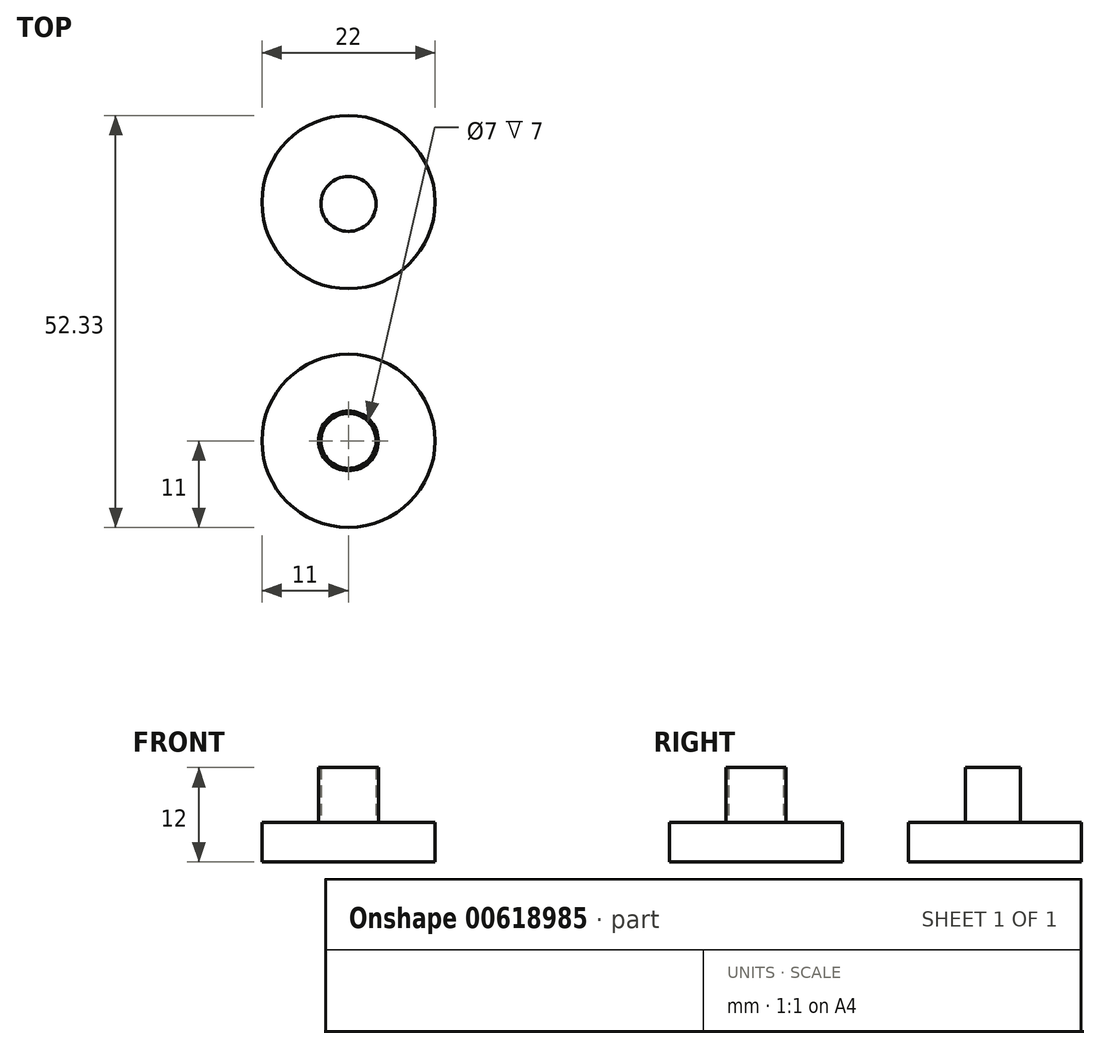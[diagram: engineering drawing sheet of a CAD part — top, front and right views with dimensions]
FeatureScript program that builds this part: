
annotation { "Feature Type Name" : "Feature", "Feature Type Description" : "" }
export const myFeature = defineFeature(function(context is Context, id is Id, definition is map)
    precondition{}
    {
        {
            var Q0;
            Q0=qCreatedBy(makeId("Top.planeOp"),FACE);
            var sketch = newSketch(context, id + "F0", { "sketchPlane" : qUnion([Q0])});
            skCircle(sketch, "E0", {"center": v(0, 0) * mm, "radius": 11 * mm});
            skCircle(sketch, "E1", {"center": v(0, 30.33) * mm, "radius": 11 * mm});
            skSolve(sketch);
        }
        {
            var Q0;
            Q0 = qSketchRegion(id + "F0", true);
            extrude(context, id + "F1", {"entities" : qUnion([Q0]), "depth" : 5 * mm, "offsetDistance" : 25 * mm});
        }
        {
            var Q0;
            Q0=qCreatedBy(makeId("Top.planeOp"),FACE);
            var sketch = newSketch(context, id + "F2", { "sketchPlane" : qUnion([Q0])});
            skCircle(sketch, "E2", {"center": v(0, 0) * mm, "radius": 3.8 * mm});
            skCircle(sketch, "E3", {"center": v(0, 0) * mm, "radius": 3.5 * mm});
            skSolve(sketch);
        }
        {
            var Q0;
            Q0 = qSketchRegion(id + "F2", true);
            extrude(context, id + "F3", {"entities" : qUnion([Q0]), "operationType" : NewBodyOperationType.ADD, "depth" : 12 * mm, "offsetDistance" : 25 * mm});
        }
        {
            var Q0;
            Q0=qCreatedBy(makeId("Top.planeOp"),FACE);
            var sketch = newSketch(context, id + "F4", { "sketchPlane" : qUnion([Q0])});
            skCircle(sketch, "E4", {"center": v(0, 30.1) * mm, "radius": 3.5 * mm});
            skSolve(sketch);
        }
        {
            var Q0;
            Q0 = qSketchRegion(id + "F4", true);
            extrude(context, id + "F5", {"entities" : qUnion([Q0]), "operationType" : NewBodyOperationType.ADD, "depth" : 12 * mm, "offsetDistance" : 25 * mm});
        }
    });
